# Revit family: Domotics-DomesticRanges-GEWISS-CHORUS_DATA-SOCKET-OUTLET_TV+SAT
name_source: partatom
category: Apparecchi elettrici
revit_build: Autodesk Revit 2016 (Build: 20161004_0715(x64)
units: mm (PartAtom-declared; Revit-internal decimal feet)

## family parameters
Condiviso = Sì
Host = Superficie
Mantenere orientamento annotazione = Sì
Punto di calcolo locali = Sì
Quota connettore circolare = Usa diametro
Taglio con vuoti quando caricato = Sì
Tipo di parte = Normale

## types (3) — shared parameters
Altezza_lampada = 45 mm  [stored 0.147638 ft]
Attenuation = 0 dB
Cable fixing = With screw
Case = Pressure casting zamak metal body
Catalogue = DOMOTICS
Catalogue Range = CHORUS - DOMESTIC RANGE
Category = TV/SAT socket-outlet
Connectors = TV-SAT
Description. = TV/SAT socket-outlet
Description: = Direct
Electrocod = 0131
IDF = faab5151-17db-460e-8ecf-96d3666eb124
IDT = 4ecf4403-10c6-4ac3-b6bb-b484be3363eb
Immagine tipo = GW14383.jpg
Larghezza_lampada = 23 mm  [stored 0.0754593 ft]
No. Chorus modules: = 2
Produttore = GEWISS S.p.A.
Prospetto di default = 1219 mm
SEO = Socket outlet
Standard; = EN 60728-4; IEC 61169-2; IEC 61169-24
Technical sheet = https://www.gewiss.com
Tipo_ = CHORUS PRESE TV-FM : GW14383 Presa TV+SAT 2M titanio
URL = https://www.gewiss.com
Version file RFA = 19.0
finitura = GEWISS NERO

## per-type parameters (varying)
| type | Colour | Descrizione | EAN code | Modello |
| GW14383 - TV+SAT 2M SOCKET TITANIUM | Titanium | TV+SAT 2M SOCKET TITANIUM | 8011564295025 | GW14383 |
| GW10383 - TV+SAT 2M SOCKET WHITE | White | TV+SAT 2M SOCKET WHITE | 8011564294950 | GW10383 |
| GW12383 - TV+SAT 2M SOCKET BLACK | Black | TV+SAT 2M SOCKET BLACK | 8011564294981 | GW12383 |

note: [stored X ft] marks values corroborated as IEEE doubles in the binary element streams (Revit-internal decimal feet)

## geometry (parser evidence)
native form markers: Sweep x1
no freeform markers — native parametric forms only
